# Revit family: Skylight-Wasco-EC-Standard_Unit
name_source: partatom
category: Windows
revit_build: Autodesk Revit Architecture 2013 (Build: 20130531_2115(x64)
units: mm (PartAtom-declared; Revit-internal decimal feet)

## types (19) — shared parameters
Acrylic Glazing Inner = Acrylic - Wasco - Clear
Acrylic Glazing Outer = Acrylic - Wasco - Clear
Curb = Rubber, Black
Curb Height = 0' - 3 1/2"
Curb Width = 0' - 1 1/2"
Default Elevation = 0' - 0"
Description = Skylight
Finish = Aluminum - Wasco - Aged Copper
Host Constraint = 1
Manufacturer = Wasco
Overhang = 0' - 1 25/32"
Product Documentation Link = http://www.wascoskylights.com
Product Name = EC Standard Unit
Product Page URL = http://www.wascoskylights.com
Type Comments = Maximum length and width = 78in x 78in.  Long leg to short leg maximum ratio cannot be more than 2.3.
URL = http://www.wascoskylights.com

## per-type parameters (varying)
| type | Height | Host Length | Host Width | L | Length | R | Rough Height | Rough Length | Rough Width | S | Width |
| EC2424 | 0' - 1 27/32" | 3' - 10" | 3' - 10" | 0' - 9 1/2" | 1' - 10" | 2' - 1 11/32" | 0' - 6 9/16" | 1' - 11 25/32" | 1' - 11 25/32" | 0' - 1 27/32" | 1' - 10" |
| EC2828 | 0' - 2 5/32" | 4' - 1 1/4" | 4' - 1 1/4" | 0' - 11 1/8" | 2' - 1 1/4" | 2' - 5 21/32" | 0' - 6 7/8" | 2' - 3 1/32" | 2' - 3 1/32" | 0' - 2 5/32" | 2' - 1 1/4" |
| EC2836 | 0' - 2 5/32" | 4' - 9 1/4" | 4' - 1 1/4" | 0' - 11 1/8" | 2' - 9 1/4" | 2' - 5 21/32" | 0' - 6 7/8" | 2' - 11 1/32" | 2' - 3 1/32" | 0' - 2 5/32" | 2' - 1 1/4" |
| EC2852 | 0' - 2 5/32" | 6' - 1 1/4" | 4' - 1 1/4" | 0' - 11 1/8" | 4' - 1 1/4" | 2' - 5 21/32" | 0' - 6 7/8" | 4' - 3 1/32" | 2' - 3 1/32" | 0' - 2 5/32" | 2' - 1 1/4" |
| EC3636 | 0' - 2 15/16" | 4' - 9 1/4" | 4' - 9 1/4" | 1' - 3 1/8" | 2' - 9 1/4" | 3' - 4 11/32" | 0' - 7 21/32" | 2' - 11 1/32" | 2' - 11 1/32" | 0' - 2 15/16" | 2' - 9 1/4" |
| EC3652 | 0' - 2 15/16" | 6' - 0 1/4" | 4' - 9 1/4" | 1' - 3 1/8" | 4' - 0 1/4" | 3' - 4 11/32" | 0' - 7 21/32" | 4' - 2 1/32" | 2' - 11 1/32" | 0' - 2 15/16" | 2' - 9 1/4" |
| EC3676 | 0' - 2 15/16" | 8' - 0 1/2" | 4' - 9 1/4" | 1' - 3 1/8" | 6' - 0 1/2" | 3' - 4 11/32" | 0' - 7 21/32" | 6' - 2 9/32" | 2' - 11 1/32" | 0' - 2 15/16" | 2' - 9 1/4" |
| EC4242 | 0' - 3 19/32" | 5' - 4" | 5' - 4" | 1' - 6 1/2" | 3' - 4" | 4' - 1 11/32" | 0' - 8 5/16" | 3' - 5 25/32" | 3' - 5 25/32" | 0' - 3 19/32" | 3' - 4" |
| EC4280 | 0' - 3 19/32" | 8' - 6" | 5' - 4" | 1' - 6 1/2" | 6' - 6" | 4' - 1 11/32" | 0' - 8 5/16" | 6' - 7 25/32" | 3' - 5 25/32" | 0' - 3 19/32" | 3' - 4" |
| EC5252 | 0' - 4 1/2" | 6' - 1 1/4" | 6' - 1 1/4" | 1' - 11 1/8" | 4' - 1 1/4" | 5' - 1 21/32" | 0' - 9 7/32" | 4' - 3 1/32" | 4' - 3 1/32" | 0' - 4 1/2" | 4' - 1 1/4" |
| EC5276 | 0' - 4 1/2" | 8' - 0 1/2" | 6' - 1 1/4" | 1' - 11 1/8" | 6' - 0 1/2" | 5' - 1 21/32" | 0' - 9 7/32" | 6' - 2 9/32" | 4' - 3 1/32" | 0' - 4 1/2" | 4' - 1 1/4" |
| EC5296 | 0' - 4 1/2" | 9' - 8 1/2" | 6' - 1 1/4" | 1' - 11 1/8" | 7' - 8 1/2" | 5' - 1 21/32" | 0' - 9 7/32" | 7' - 10 9/32" | 4' - 3 1/32" | 0' - 4 1/2" | 4' - 1 1/4" |
| EC5555 | 0' - 4 21/32" | 6' - 3" | 6' - 3" | 2' - 0" | 4' - 3" | 5' - 4" | 0' - 9 3/8" | 4' - 4 25/32" | 4' - 4 25/32" | 0' - 4 21/32" | 4' - 3" |
| EC55102 | 0' - 4 21/32" | 10' - 3" | 6' - 3" | 2' - 0" | 8' - 3" | 5' - 4" | 0' - 9 3/8" | 8' - 4 25/32" | 4' - 4 25/32" | 0' - 4 21/32" | 4' - 3" |
| EC6060 | 0' - 5 11/32" | 6' - 10" | 6' - 10" | 2' - 3 1/2" | 4' - 10" | 6' - 1 11/32" | 0' - 10 1/16" | 4' - 11 25/32" | 4' - 11 25/32" | 0' - 5 11/32" | 4' - 10" |
| EC6476 | 0' - 5 19/32" | 8' - 0 1/2" | 7' - 0 1/2" | 2' - 4 3/4" | 6' - 0 1/2" | 6' - 4 21/32" | 0' - 10 5/16" | 6' - 2 9/32" | 5' - 2 9/32" | 0' - 5 19/32" | 5' - 0 1/2" |
| EC6496 | 0' - 5 19/32" | 9' - 8 1/2" | 7' - 0 1/2" | 2' - 4 3/4" | 7' - 8 1/2" | 6' - 4 21/32" | 0' - 10 5/16" | 7' - 10 9/32" | 5' - 2 9/32" | 0' - 5 19/32" | 5' - 0 1/2" |
| EC7272 | 0' - 6 5/8" | 7' - 11" | 7' - 11" | 2' - 10" | 5' - 11" | 7' - 6 21/32" | 0' - 11 11/32" | 6' - 0 25/32" | 6' - 0 25/32" | 0' - 6 5/8" | 5' - 11" |
| Custom | 0' - 4 3/8" | 6' - 0" | 6' - 0" | 1' - 10 1/2" | 4' - 0" | 5' - 0" | 0' - 9 3/32" | 4' - 1 25/32" | 4' - 1 25/32" | 0' - 4 3/8" | 4' - 0" |

note: column(s) folded — value = type name in every type: Model

## geometry (parser evidence)
native form markers: Blend x24, Extrusion x1, Sweep x3
no freeform markers — native parametric forms only
